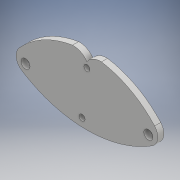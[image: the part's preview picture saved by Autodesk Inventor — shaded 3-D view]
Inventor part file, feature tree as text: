
AUTODESK INVENTOR PART (.ipt)
format: ipt  version: 2018 (Build 220112000, 112)  size: 135,168 bytes
history: native  units: mm
features: extrude x4, sketch x4, fillet x1
ambient origin geometry x8: Origin, YZ Plane, XZ Plane, XY Plane, X Axis, Y Axis, Z Axis, Center Point
bodies: Solid1 (feature_tree)
feature tree (9):
  extrude  "Extrusion1"  Depth=20.0mm
  fillet  "Fillet1"  Radius=15.0mm
  extrude  "Extrusion2"  Depth=2.0mm
  extrude  "Extrusion3"  Depth=1.0mm
  extrude  "Extrusion4"  Depth=1.0mm
  sketch  "Sketch1"  dims[d0=25.0mm d1=20.0mm d2=15.0mm]
  sketch  "Sketch2"  dims[d3=1.0mm d4=0.0mm d5=2.0mm]
  sketch  "Sketch3"  dims[d7=1.0mm d8=0.0mm d10=1.5mm]
  sketch  "Sketch4"  dims[d11=1.5mm d12=1.5mm d13=1.5mm d14=1.0mm d15=1.0mm d16=0.0mm d17=1.0mm d18=1.0mm d19=0.0mm]
